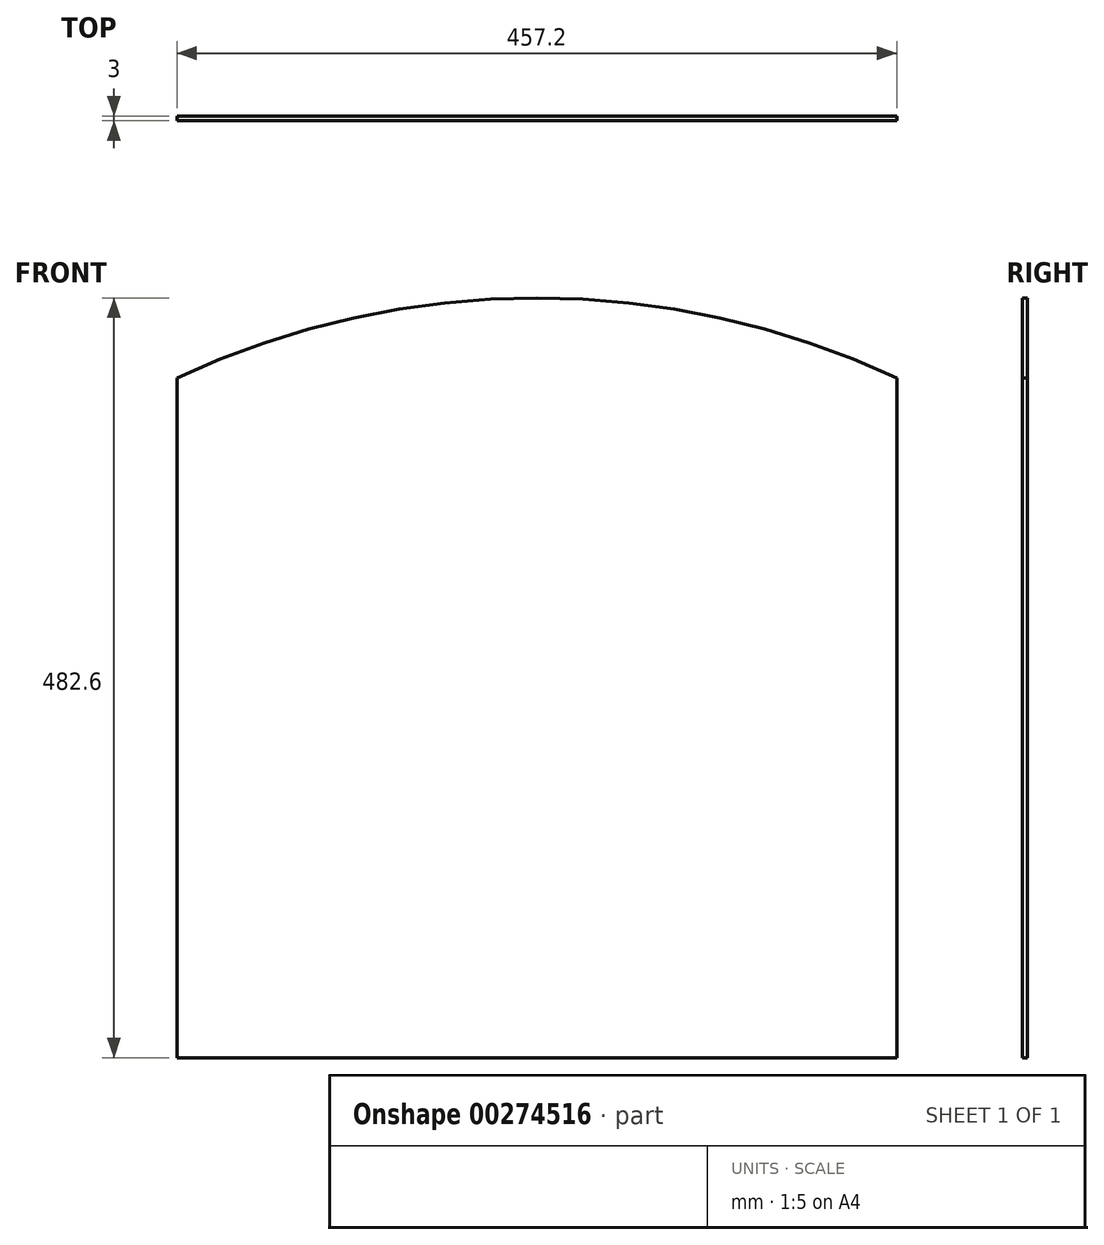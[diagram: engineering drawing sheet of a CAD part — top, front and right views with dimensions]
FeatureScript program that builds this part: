
annotation { "Feature Type Name" : "Feature", "Feature Type Description" : "" }
export const myFeature = defineFeature(function(context is Context, id is Id, definition is map)
    precondition{}
    {
        {
            var Q0;
            Q0=qCreatedBy(makeId("Front.planeOp"),FACE);
            var sketch = newSketch(context, id + "F0", { "sketchPlane" : qUnion([Q0])});
            skLineSegment(sketch, "E0.bottom", {"start": v(-228.6, -329.4) * mm, "end": v(228.6, -329.4) * mm});
            skLineSegment(sketch, "E0.left", {"start": v(-228.6, -329.4) * mm, "end": v(-228.6, 102.4) * mm});
            skLineSegment(sketch, "E0.right", {"start": v(228.6, -329.4) * mm, "end": v(228.6, 102.4) * mm});
            skPoint(sketch, "E1", {"position": v(0, 153.2) * mm});
            skArc(sketch, "E2", {"start": v(228.6, 102.4) * mm, "mid": v(0, 153.2) * mm, "end": v(-228.6, 102.4) * mm});
            skSolve(sketch);
        }
        {
            var Q0;
            Q0 = qSketchRegion(id + "F0", true);
            extrude(context, id + "F1", {"entities" : qUnion([Q0]), "depth" : 3 * mm});
        }
    });
